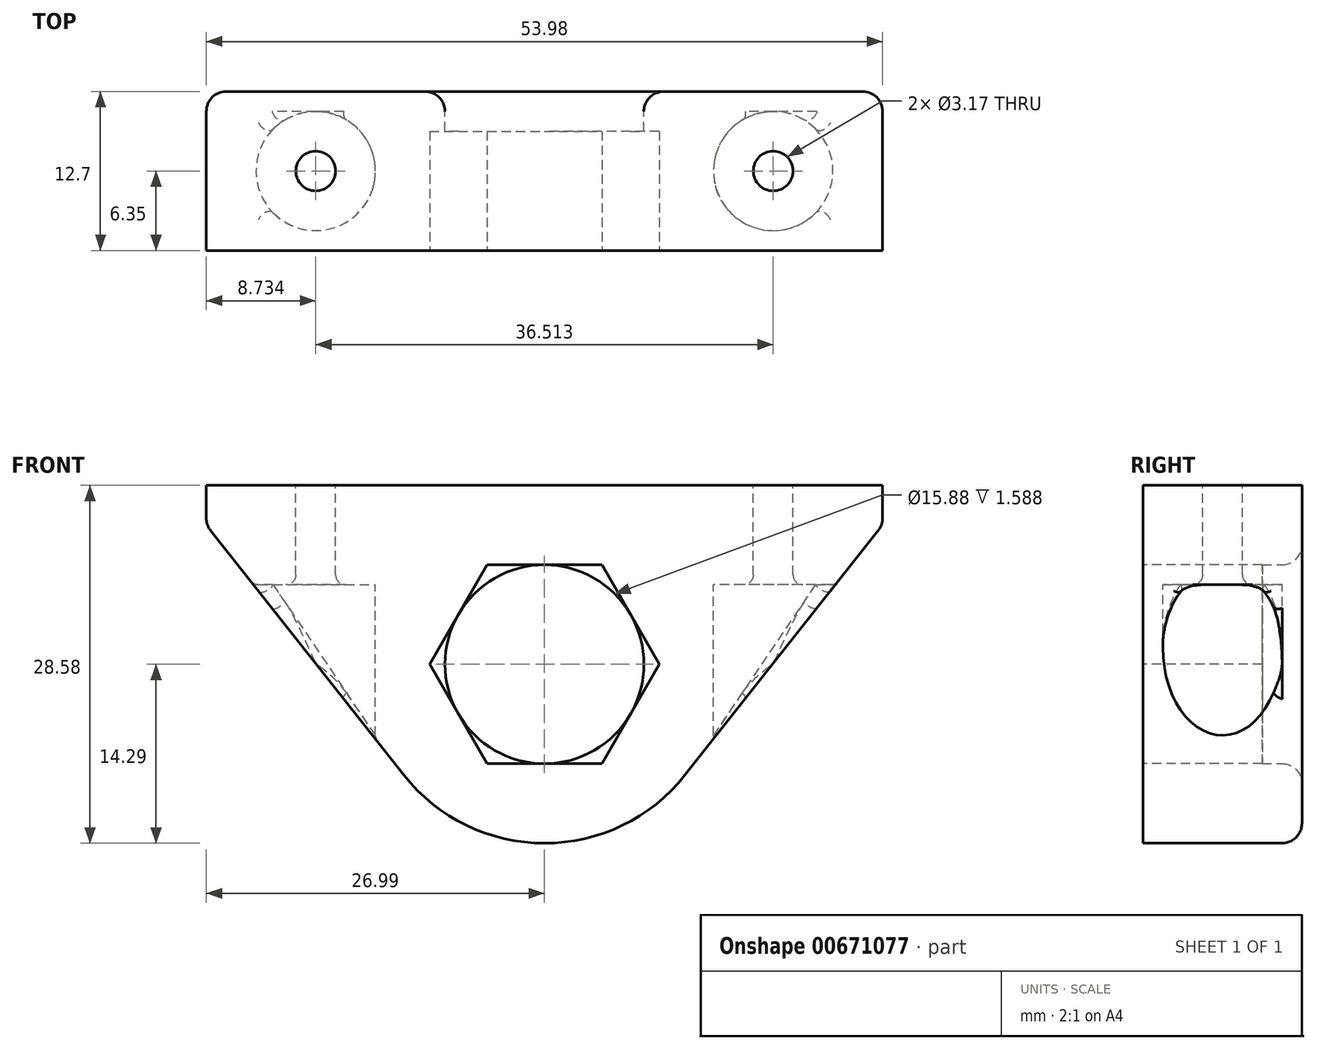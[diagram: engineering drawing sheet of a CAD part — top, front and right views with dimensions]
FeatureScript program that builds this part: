
annotation { "Feature Type Name" : "Feature", "Feature Type Description" : "" }
export const myFeature = defineFeature(function(context is Context, id is Id, definition is map)
    precondition{}
    {
        {
            var Q0;
            Q0=qCreatedBy(makeId("Front.planeOp"),FACE);
            var sketch = newSketch(context, id + "F0", { "sketchPlane" : qUnion([Q0])});
            skCircle(sketch, "E0", {"center": v(0, 0) * mm, "radius": 14.29 * mm});
            skCircle(sketch, "E1", {"center": v(0, 0) * mm, "radius": 7.94 * mm});
            skLineSegment(sketch, "E2", {"start": v(-11.21, -8.86) * mm, "end": v(-26.99, 11.11) * mm});
            skLineSegment(sketch, "E3", {"start": v(-26.99, 11.11) * mm, "end": v(26.99, 11.11) * mm});
            skLineSegment(sketch, "E4", {"start": v(26.99, 11.11) * mm, "end": v(11.21, -8.86) * mm});
            skLineSegment(sketch, "E5", {"start": v(0, 0) * mm, "end": v(0, 22.65) * mm, "construction": true});
            skLineSegment(sketch, "E6.top", {"start": v(-26.99, 14.29) * mm, "end": v(26.99, 14.29) * mm});
            skLineSegment(sketch, "E6.left", {"start": v(-26.99, 11.11) * mm, "end": v(-26.99, 14.29) * mm});
            skLineSegment(sketch, "E6.right", {"start": v(26.99, 11.11) * mm, "end": v(26.99, 14.29) * mm});
            skSolve(sketch);
        }
        {
            var Q0;
            Q0=qSketchRegion(id+"F0",true);
            extrude(context, id + "F1", {"entities" : qUnion([Q0]), "depth" : 12.7 * mm, "offsetDistance" : 25.4 * mm});
        }
        {
            var Q0;
            Q0=makeQuery(id+"F1.opExtrude","CAP_FACE",FACE,{"disambiguationData":[OSD([sQuery(id+"F0.wireOp",EDGE,"E0"),sQuery(id+"F0.wireOp",EDGE,"E1"),sQuery(id+"F0.wireOp",EDGE,"E2"),sQuery(id+"F0.wireOp",EDGE,"E4"),sQuery(id+"F0.wireOp",EDGE,"E6.top"),sQuery(id+"F0.wireOp",EDGE,"E6.left"),sQuery(id+"F0.wireOp",EDGE,"E6.right")])],"isStart":false});
            var sketch = newSketch(context, id + "F2", { "sketchPlane" : qUnion([Q0])});
            skCircle(sketch, "E7.0", {"center": v(0, 0) * mm, "radius": 7.94 * mm, "construction": true});
            skLineSegment(sketch, "E8.0", {"start": v(-4.58, 7.94) * mm, "end": v(4.58, 7.94) * mm});
            skLineSegment(sketch, "E8.1", {"start": v(4.58, 7.94) * mm, "end": v(9.17, 0) * mm});
            skLineSegment(sketch, "E8.2", {"start": v(9.17, 0) * mm, "end": v(4.58, -7.94) * mm});
            skLineSegment(sketch, "E8.3", {"start": v(4.58, -7.94) * mm, "end": v(-4.58, -7.94) * mm});
            skLineSegment(sketch, "E8.4", {"start": v(-4.58, -7.94) * mm, "end": v(-9.17, 0) * mm});
            skLineSegment(sketch, "E8.5", {"start": v(-9.17, 0) * mm, "end": v(-4.58, 7.94) * mm});
            skPoint(sketch, "E8.0.midPoint", {"position": v(0, 7.94) * mm});
            skSolve(sketch);
        }
        {
            var Q0;
            Q0=qSketchRegion(id+"F2",true);
            extrude(context, id + "F3", {"entities" : qUnion([Q0]), "operationType" : NewBodyOperationType.REMOVE, "oppositeDirection" : true, "depth" : 9.52 * mm, "offsetDistance" : 25.4 * mm});
        }
        {
            var Q0;
            Q0=makeQuery(id+"F1.opExtrude","CAP_EDGE",EDGE,{"disambiguationData":[OSD([sQuery(id+"F0.wireOp",EDGE,"E4")])],"isStart":true});
            var Q1;
            Q1=makeQuery(id+"F1.opExtrude","SWEPT_EDGE",EDGE,{"disambiguationData":[OSD([sQuery(id+"F0.wireOp",EDGE,"E4"),sQuery(id+"F0.wireOp",EDGE,"E3"),sQuery(id+"F0.wireOp",EDGE,"E6.right")])]});
            var Q2;
            Q2=makeQuery(id+"F1.opExtrude","SWEPT_EDGE",EDGE,{"disambiguationData":[OSD([sQuery(id+"F0.wireOp",EDGE,"E2"),sQuery(id+"F0.wireOp",EDGE,"E3"),sQuery(id+"F0.wireOp",EDGE,"E6.left")])]});
            var Q3;
            Q3=makeQuery(id+"F1.opExtrude","CAP_EDGE",EDGE,{"disambiguationData":[OSD([sQuery(id+"F0.wireOp",EDGE,"E6.left")])],"isStart":true});
            var Q4;
            Q4=makeQuery(id+"F1.opExtrude","CAP_EDGE",EDGE,{"disambiguationData":[OSD([sQuery(id+"F0.wireOp",EDGE,"E6.right")])],"isStart":true});
            var Q5;
            Q5=makeQuery(id+"F1.opExtrude","CAP_EDGE",EDGE,{"disambiguationData":[OSD([sQuery(id+"F0.wireOp",EDGE,"E1")])],"isStart":true});
            fillet(context, id + "F4", {"entities" : qUnion([Q0, Q1, Q2, Q3, Q4, Q5]), "radius" : 1.59 * mm, "tangentPropagation" : true, "allowEdgeOverflow" : false});
        }
        {
            var Q0;
            Q0=makeQuery(id+"F1.opExtrude","SWEPT_FACE",FACE,{"disambiguationData":[OSD([sQuery(id+"F0.wireOp",EDGE,"E6.top")])]});
            var sketch = newSketch(context, id + "F5", { "sketchPlane" : qUnion([Q0])});
            skLineSegment(sketch, "E9", {"start": v(-9.49, -14.29) * mm, "end": v(-9.49, 1.59) * mm, "construction": true});
            skLineSegment(sketch, "E10", {"start": v(9.53, -1.59) * mm, "end": v(9.53, -17.46) * mm, "construction": true});
            skCircle(sketch, "E11", {"center": v(-18.26, -6.35) * mm, "radius": 1.59 * mm});
            skLineSegment(sketch, "E12", {"start": v(-9.49, -6.35) * mm, "end": v(-18.26, -6.35) * mm, "construction": true});
            skCircle(sketch, "E13.MirrorC", {"center": v(18.26, -6.35) * mm, "radius": 1.59 * mm});
            skLineSegment(sketch, "E14", {"start": v(-18.26, -12.7) * mm, "end": v(-18.26, 0) * mm, "construction": true});
            skSolve(sketch);
        }
        {
            var Q0;
            Q0=qSketchRegion(id+"F5",true);
            extrude(context, id + "F6", {"entities" : qUnion([Q0]), "operationType" : NewBodyOperationType.REMOVE, "endBound" : BoundingType.THROUGH_ALL, "oppositeDirection" : true, "depth" : 25.4 * mm, "offsetDistance" : 25.4 * mm});
        }
        {
            var Q0;
            Q0=qCreatedBy(makeId("Top.planeOp"),FACE);
            var sketch = newSketch(context, id + "F7", { "sketchPlane" : qUnion([Q0])});
            skCircle(sketch, "E15.0", {"center": v(18.26, -6.35) * mm, "radius": 1.59 * mm, "construction": true});
            skCircle(sketch, "E16", {"center": v(18.26, -6.35) * mm, "radius": 4.76 * mm});
            skCircle(sketch, "E17.MirrorC", {"center": v(-18.26, -6.35) * mm, "radius": 4.76 * mm});
            skSolve(sketch);
        }
        {
            var Q0;
            Q0=qSketchRegion(id+"F7",true);
            extrude(context, id + "F8", {"entities" : qUnion([Q0]), "operationType" : NewBodyOperationType.REMOVE, "endBound" : BoundingType.THROUGH_ALL, "oppositeDirection" : true, "depth" : 25.4 * mm, "offsetDistance" : 25.4 * mm, "hasSecondDirection" : true, "secondDirectionOppositeDirection" : false, "secondDirectionDepth" : 6.35 * mm});
        }
        {
            var Q0;
            Q0=makeQuery(id+"F8.boolean.opBoolean","INTERSECT",EDGE,{"derivedFrom":[makeQuery(id+"F1.opExtrude","SWEPT_FACE",FACE,{"disambiguationData":[OSD([sQuery(id+"F0.wireOp",EDGE,"E2")])]}),makeQuery(id+"F8.opExtrude","SWEPT_FACE",FACE,{"disambiguationData":[OSD([sQuery(id+"F7.wireOp",EDGE,"E17.MirrorC")])]})]});
            var Q1;
            Q1=makeQuery(id+"F8.boolean.opBoolean","INTERSECT",EDGE,{"derivedFrom":[makeQuery(id+"F1.opExtrude","SWEPT_FACE",FACE,{"disambiguationData":[OSD([sQuery(id+"F0.wireOp",EDGE,"E4")])]}),makeQuery(id+"F8.opExtrude","SWEPT_FACE",FACE,{"disambiguationData":[OSD([sQuery(id+"F7.wireOp",EDGE,"E16")])]})]});
            var Q2;
            Q2=makeQuery(id+"F6.boolean.opBoolean","COPY",EDGE,{"derivedFrom":makeQuery(id+"F6.opExtrude","CAP_EDGE",EDGE,{"disambiguationData":[OSD([sQuery(id+"F5.wireOp",EDGE,"E11")])],"isStart":true})});
            var Q3;
            Q3=makeQuery(id+"F6.boolean.opBoolean","COPY",EDGE,{"derivedFrom":makeQuery(id+"F6.opExtrude","CAP_EDGE",EDGE,{"disambiguationData":[OSD([sQuery(id+"F5.wireOp",EDGE,"E13.MirrorC")])],"isStart":true})});
            var Q4;
            Q4=makeQuery(id+"F8.boolean.opBoolean","INTERSECT",EDGE,{"derivedFrom":[makeQuery(id+"F6.boolean.opBoolean","COPY",FACE,{"derivedFrom":makeQuery(id+"F6.opExtrude","SWEPT_FACE",FACE,{"disambiguationData":[OSD([sQuery(id+"F5.wireOp",EDGE,"E11")])]})}),makeQuery(id+"F8.opExtrude","CAP_FACE",FACE,{"disambiguationData":[OSD([sQuery(id+"F7.wireOp",EDGE,"E17.MirrorC")])],"isStart":true})]});
            var Q5;
            Q5=makeQuery(id+"F8.boolean.opBoolean","INTERSECT",EDGE,{"derivedFrom":[makeQuery(id+"F6.boolean.opBoolean","COPY",FACE,{"derivedFrom":makeQuery(id+"F6.opExtrude","SWEPT_FACE",FACE,{"disambiguationData":[OSD([sQuery(id+"F5.wireOp",EDGE,"E13.MirrorC")])]})}),makeQuery(id+"F8.opExtrude","CAP_FACE",FACE,{"disambiguationData":[OSD([sQuery(id+"F7.wireOp",EDGE,"E16")])],"isStart":true})]});
            var Q6;
            Q6=makeQuery(id+"F3.boolean.opBoolean","COPY",EDGE,{"derivedFrom":makeQuery(id+"F3.opExtrude","CAP_EDGE",EDGE,{"disambiguationData":[OSD([sQuery(id+"F2.wireOp",EDGE,"JiJy6y8C-PNO4-eTD7-m4Dv-ocb9p2OpqMhO")])],"isStart":true})});
            fillet(context, id + "F9", {"entities" : qUnion([Q0, Q1, Q2, Q3, Q4, Q5, Q6]), "radius" : 0.8 * mm, "tangentPropagation" : true, "allowEdgeOverflow" : false});
        }
    });
